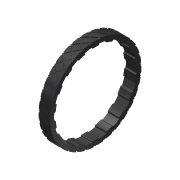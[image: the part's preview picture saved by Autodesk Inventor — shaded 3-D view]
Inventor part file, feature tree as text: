
AUTODESK INVENTOR PART (.ipt)
format: ipt  version: 2013 (Build 170138000, 138)  size: 1,437,696 bytes
history: native  units: in
note: dims shown in document units (in); Inventor stores cm internally (conversion verified against a paired STEP export)
features: pattern_circular x1, extrude x1, mirror x1, imported_body x1, sketch x1
ambient origin geometry x8: Origin, YZ Plane, XZ Plane, XY Plane, X Axis, Y Axis, Z Axis, Center Point
feature tree (5):
  pattern_circular  "CirPattern4"
  extrude  "Extrusion1"  Depth=0.5in TaperAngle=0.0deg
  mirror  "Mirror1"
  imported_body  "Base1"
  sketch  "Sketch1"  dims[d0=8.5in d1=0.5in d2=0.0in]
